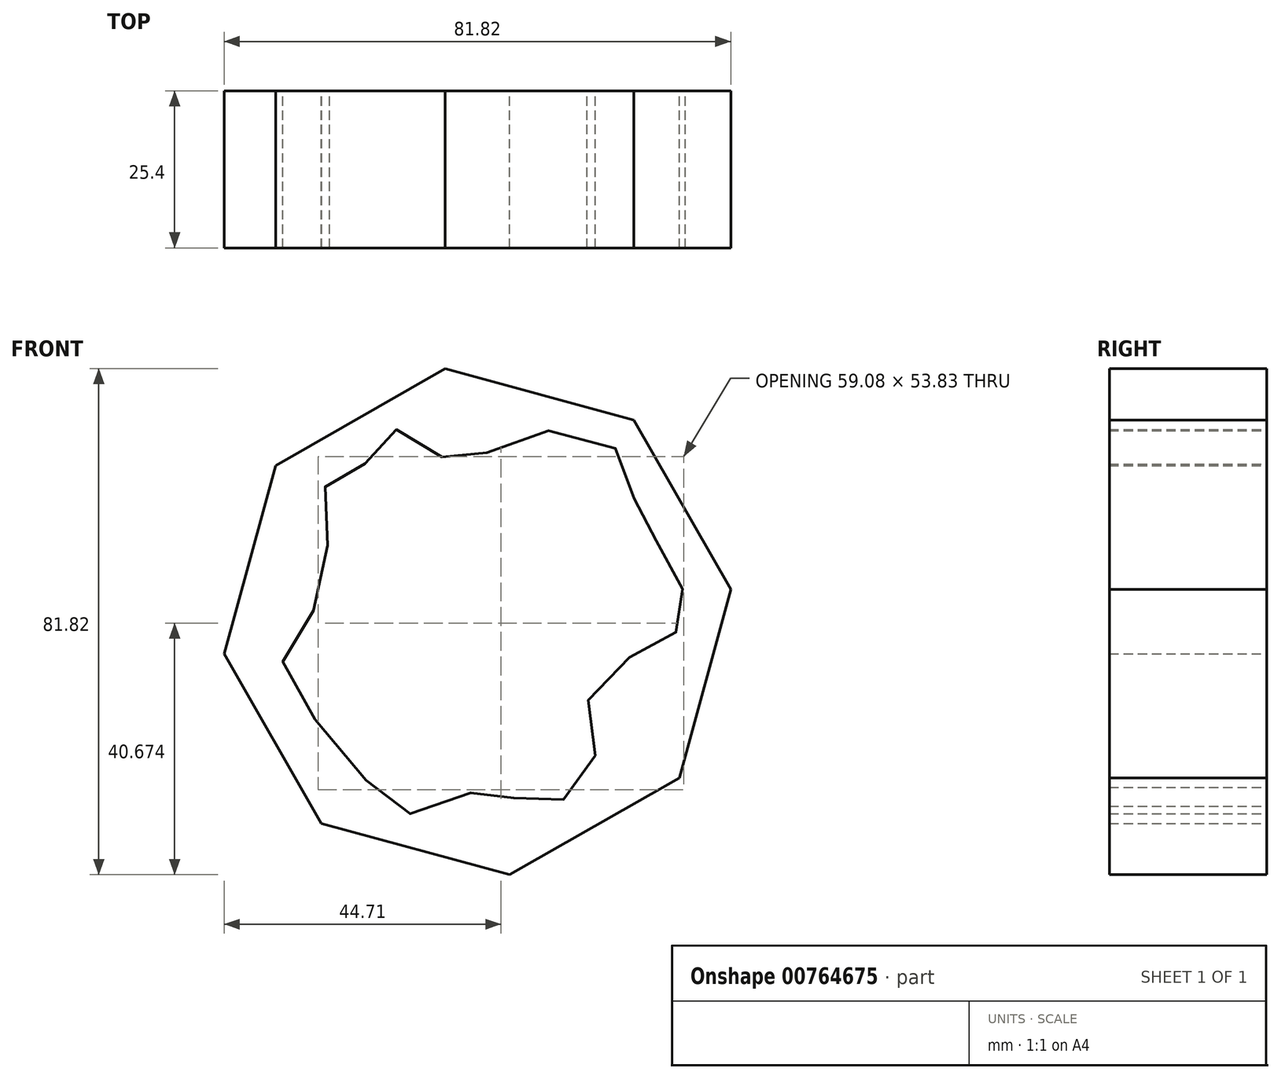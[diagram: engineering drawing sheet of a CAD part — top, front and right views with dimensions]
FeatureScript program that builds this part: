
annotation { "Feature Type Name" : "Feature", "Feature Type Description" : "" }
export const myFeature = defineFeature(function(context is Context, id is Id, definition is map)
    precondition{}
    {
        {
            var Q0;
            Q0=qCreatedBy(makeId("Front.planeOp"),FACE);
            var sketch = newSketch(context, id + "F0", { "sketchPlane" : qUnion([Q0])});
            skCircle(sketch, "E0.cCircle", {"center": v(0, 0) * mm, "radius": 38.1 * mm, "construction": true});
            skLineSegment(sketch, "E0.0", {"start": v(-32.61, 25.24) * mm, "end": v(-5.21, 40.9) * mm});
            skLineSegment(sketch, "E0.1", {"start": v(-5.21, 40.9) * mm, "end": v(25.24, 32.61) * mm});
            skLineSegment(sketch, "E0.2", {"start": v(25.24, 32.61) * mm, "end": v(40.9, 5.21) * mm});
            skLineSegment(sketch, "E0.3", {"start": v(40.9, 5.21) * mm, "end": v(32.61, -25.24) * mm});
            skLineSegment(sketch, "E0.4", {"start": v(32.61, -25.24) * mm, "end": v(5.21, -40.9) * mm});
            skLineSegment(sketch, "E0.5", {"start": v(5.21, -40.9) * mm, "end": v(-25.24, -32.61) * mm});
            skLineSegment(sketch, "E0.6", {"start": v(-25.24, -32.61) * mm, "end": v(-40.9, -5.21) * mm});
            skLineSegment(sketch, "E0.7", {"start": v(-40.9, -5.21) * mm, "end": v(-32.61, 25.24) * mm});
            skPoint(sketch, "E0.0.midPoint", {"position": v(-18.91, 33.08) * mm});
            skPoint(sketch, "E1", {"position": v(-1.75, 13.55) * mm});
            skPoint(sketch, "E2", {"position": v(8.2, 26.45) * mm});
            skPoint(sketch, "E3", {"position": v(12.63, 14.47) * mm});
            skPoint(sketch, "E4", {"position": v(-18.16, 25.53) * mm});
            skPoint(sketch, "E5", {"position": v(-20.74, 12.08) * mm});
            skPoint(sketch, "E6", {"position": v(-12.63, 25.72) * mm});
            skPoint(sketch, "E7", {"position": v(-13.18, 13.55) * mm});
            skPoint(sketch, "E8", {"position": v(-5.21, 40.9) * mm});
            skPoint(sketch, "E9", {"position": v(-3.23, 26.45) * mm});
            skPoint(sketch, "E10", {"position": v(20.37, 16.87) * mm});
            skPoint(sketch, "E11", {"position": v(18.34, 25.16) * mm});
            skPoint(sketch, "E12", {"position": v(6.36, -9.86) * mm});
            skPoint(sketch, "E13", {"position": v(0.65, -13.18) * mm});
            skPoint(sketch, "E14", {"position": v(-23.69, -2.12) * mm});
            skPoint(sketch, "E15", {"position": v(2.12, 2.86) * mm});
            skPoint(sketch, "E16", {"position": v(8.76, -8.76) * mm});
            skPoint(sketch, "E17", {"position": v(-16.68, -13.18) * mm});
            skPoint(sketch, "E18", {"position": v(-19.27, 2.86) * mm});
            skPoint(sketch, "E19", {"position": v(-24.24, 6.18) * mm});
            skPoint(sketch, "E20", {"position": v(-14.29, 7.1) * mm});
            skPoint(sketch, "E21", {"position": v(-7.84, -2.67) * mm});
            skPoint(sketch, "E22", {"position": v(18.16, 1.75) * mm});
            skPoint(sketch, "E23", {"position": v(28.3, -2.12) * mm});
            skPoint(sketch, "E24", {"position": v(25.16, -13) * mm});
            skPoint(sketch, "E25", {"position": v(13, -19.63) * mm});
            skPoint(sketch, "E26", {"position": v(-5.8, -21.48) * mm});
            skPoint(sketch, "E27", {"position": v(0, -24.43) * mm});
            skPoint(sketch, "E28", {"position": v(20.74, 10.42) * mm});
            skFitSpline(sketch, "E29", {"points": [v(-18.16, 25.53) * mm, v(-24.8, 21.48) * mm, v(-24.24, 6.18) * mm, v(-31.43, -6.18) * mm, v(-20.74, -22.03) * mm, v(-10.78, -31.06) * mm, v(2.49, -26.82) * mm, v(8.39, -29.77) * mm, v(18.71, -24.24) * mm, v(17.8, -13) * mm, v(27.56, -4.15) * mm, v(33.28, 0) * mm, v(31.06, 10.23) * mm, v(25.9, 17.42) * mm, v(22.77, 27.56) * mm, v(5.8, 29.77) * mm, v(-3.41, 25.53) * mm, v(-12.81, 31.06) * mm, v(-18.16, 25.53) * mm]});
            skCircle(sketch, "E30", {"center": v(-12.63, 20.37) * mm, "radius": 4.79 * mm});
            skCircle(sketch, "E31", {"center": v(6.54, 20.37) * mm, "radius": 5.88 * mm});
            skCircle(sketch, "E32", {"center": v(-13.18, -1.94) * mm, "radius": 5.3 * mm});
            skCircle(sketch, "E33", {"center": v(5.25, 7.28) * mm, "radius": 5.06 * mm});
            skCircle(sketch, "E34", {"center": v(1.94, -8.02) * mm, "radius": 5.44 * mm});
            skCircle(sketch, "E35", {"center": v(24.24, 5.8) * mm, "radius": 5.07 * mm});
            skCircle(sketch, "E36", {"center": v(-13.18, -15.95) * mm, "radius": 5.53 * mm});
            skCircle(sketch, "E37", {"center": v(9.86, -22.77) * mm, "radius": 5.04 * mm});
            skSolve(sketch);
        }
        {
            var Q0;
            Q0=makeQuery(id+"F0.imprint","IMPRINT",FACE,{"disambiguationData":[TD([[makeQuery(id+"F0.imprint","IMPRINT",EDGE,{"derivedFrom":sQuery(id+"F0.wireOp",EDGE,"E0.0")}),-1.0]])]});
            extrude(context, id + "F1", {"entities" : qUnion([Q0]), "depth" : 25.4 * mm, "offsetDistance" : 25.4 * mm});
        }
    });
